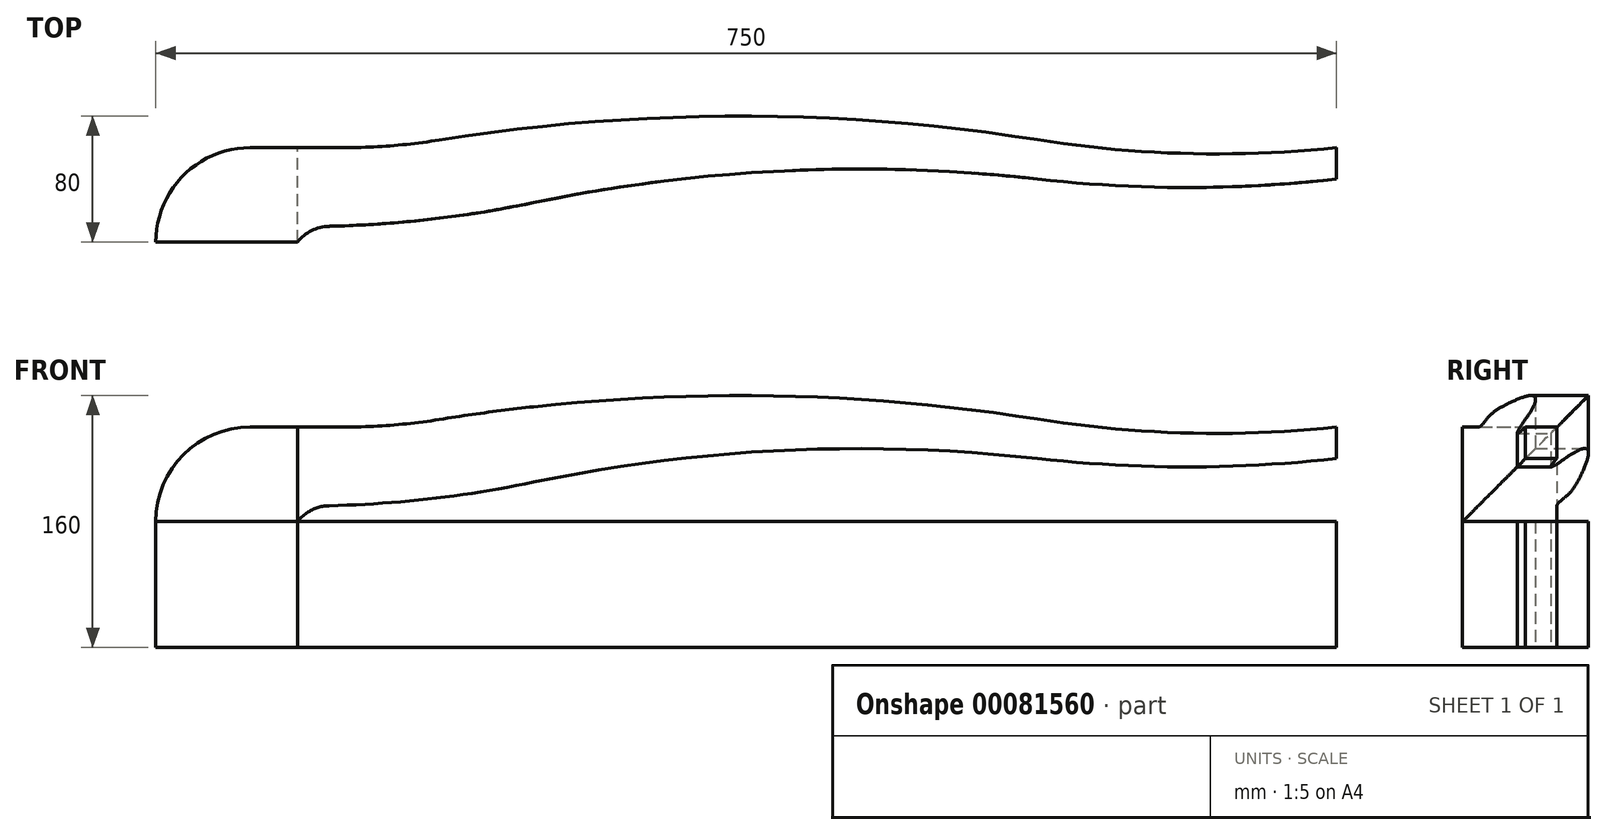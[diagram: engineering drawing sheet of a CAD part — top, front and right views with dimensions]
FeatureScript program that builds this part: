
annotation { "Feature Type Name" : "Feature", "Feature Type Description" : "" }
export const myFeature = defineFeature(function(context is Context, id is Id, definition is map)
    precondition{}
    {
        {
            var Q0;
            Q0=qCreatedBy(makeId("Front.planeOp"),FACE);
            var sketch = newSketch(context, id + "F0", { "sketchPlane" : qUnion([Q0])});
            skLineSegment(sketch, "E0.bottom", {"start": v(-375, 40) * mm, "end": v(375, 40) * mm, "construction": true});
            skLineSegment(sketch, "E0.top", {"start": v(-375, -40) * mm, "end": v(375, -40) * mm, "construction": true});
            skLineSegment(sketch, "E0.left", {"start": v(-375, 40) * mm, "end": v(-375, -40) * mm, "construction": true});
            skLineSegment(sketch, "E0.right", {"start": v(375, 40) * mm, "end": v(375, -40) * mm, "construction": true});
            skArc(sketch, "E1", {"start": v(-375, -40) * mm, "mid": v(-357.43, 2.43) * mm, "end": v(-315, 20) * mm});
            skLineSegment(sketch, "E2", {"start": v(-315, 20) * mm, "end": v(-255, 20) * mm});
            skArc(sketch, "E3", {"start": v(-255, 20) * mm, "mid": v(-224.9, 21.2) * mm, "end": v(-195, 24.79) * mm});
            skArc(sketch, "E4", {"start": v(-195, 24.79) * mm, "mid": v(-5, 40) * mm, "end": v(185, 25) * mm});
            skArc(sketch, "E5", {"start": v(185, 25) * mm, "mid": v(279.83, 16.23) * mm, "end": v(375, 20) * mm});
            skLineSegment(sketch, "E6", {"start": v(375, 20) * mm, "end": v(375, 0) * mm});
            skArc(sketch, "E7", {"start": v(375, 0) * mm, "mid": v(280, -5.33) * mm, "end": v(185, 0) * mm});
            skArc(sketch, "E8", {"start": v(185, 0) * mm, "mid": v(24.4, 5.23) * mm, "end": v(-135, -15) * mm});
            skArc(sketch, "E9", {"start": v(-135, -15) * mm, "mid": v(-199.66, -25.45) * mm, "end": v(-265, -30) * mm});
            skArc(sketch, "E10", {"start": v(-265, -30) * mm, "mid": v(-276.12, -32.77) * mm, "end": v(-285, -40) * mm});
            skLineSegment(sketch, "E11", {"start": v(-372.46, -190.94) * mm, "end": v(-262.22, 0) * mm, "construction": true});
            skLineSegment(sketch, "E12", {"start": v(-285, -40) * mm, "end": v(-375, -40) * mm});
            skSolve(sketch);
        }
        {
            var Q0;
            Q0 = qSketchRegion(id + "F0", true);
            extrude(context, id + "F1", {"entities" : qUnion([Q0]), "endBound" : BoundingType.SYMMETRIC, "depth" : 80 * mm});
        }
        {
            var Q0;
            Q0=makeQuery(id+"F1.opExtrude","SWEPT_BODY",BODY,{"disambiguationData":[OSD([sQuery(id+"F0.wireOp",EDGE,"E1"),sQuery(id+"F0.wireOp",EDGE,"E2"),sQuery(id+"F0.wireOp",EDGE,"E3"),sQuery(id+"F0.wireOp",EDGE,"E4"),sQuery(id+"F0.wireOp",EDGE,"E5"),sQuery(id+"F0.wireOp",EDGE,"E6"),sQuery(id+"F0.wireOp",EDGE,"E7"),sQuery(id+"F0.wireOp",EDGE,"E8"),sQuery(id+"F0.wireOp",EDGE,"E9"),sQuery(id+"F0.wireOp",EDGE,"E10"),sQuery(id+"F0.wireOp",EDGE,"E12")])]});
            var Q1;
            Q1=makeQuery(id+"F1.opExtrude","CAP_EDGE",EDGE,{"disambiguationData":[OSD([sQuery(id+"F0.wireOp",EDGE,"E12")])],"isStart":false});
            transform(context, id + "F2", {"entities" : qUnion([Q0]), "transformType" : TransformType.ROTATION, "transformAxis" : qUnion([Q1]), "angle" : 90 * degree, "makeCopy" : true});
        }
        {
            var Q0;
            Q0=makeQuery(id+"F2.opPattern","COPY",BODY,{"derivedFrom":makeQuery(id+"F1.opExtrude","SWEPT_BODY",BODY,{"disambiguationData":[OSD([sQuery(id+"F0.wireOp",EDGE,"E1"),sQuery(id+"F0.wireOp",EDGE,"E2"),sQuery(id+"F0.wireOp",EDGE,"E3"),sQuery(id+"F0.wireOp",EDGE,"E4"),sQuery(id+"F0.wireOp",EDGE,"E5"),sQuery(id+"F0.wireOp",EDGE,"E6"),sQuery(id+"F0.wireOp",EDGE,"E7"),sQuery(id+"F0.wireOp",EDGE,"E8"),sQuery(id+"F0.wireOp",EDGE,"E9"),sQuery(id+"F0.wireOp",EDGE,"E10"),sQuery(id+"F0.wireOp",EDGE,"E12")])]}),"instanceName":"1"});
            transform(context, id + "F3", {"entities" : qUnion([Q0]), "transformType" : TransformType.TRANSLATION_3D, "dx" : 0 * mm, "dy" : 0 * mm, "dz" : 80 * mm, "makeCopy" : true});
        }
        {
            var Q0;
            Q0=makeQuery(id+"F3.opPattern","COPY",BODY,{"derivedFrom":makeQuery(id+"F2.opPattern","COPY",BODY,{"derivedFrom":makeQuery(id+"F1.opExtrude","SWEPT_BODY",BODY,{"disambiguationData":[OSD([sQuery(id+"F0.wireOp",EDGE,"E1"),sQuery(id+"F0.wireOp",EDGE,"E2"),sQuery(id+"F0.wireOp",EDGE,"E3"),sQuery(id+"F0.wireOp",EDGE,"E4"),sQuery(id+"F0.wireOp",EDGE,"E5"),sQuery(id+"F0.wireOp",EDGE,"E6"),sQuery(id+"F0.wireOp",EDGE,"E7"),sQuery(id+"F0.wireOp",EDGE,"E8"),sQuery(id+"F0.wireOp",EDGE,"E9"),sQuery(id+"F0.wireOp",EDGE,"E10"),sQuery(id+"F0.wireOp",EDGE,"E12")])]}),"instanceName":"1"}),"instanceName":"1"});
            var Q1;
            Q1=makeQuery(id+"F1.opExtrude","SWEPT_BODY",BODY,{"disambiguationData":[OSD([sQuery(id+"F0.wireOp",EDGE,"E1"),sQuery(id+"F0.wireOp",EDGE,"E2"),sQuery(id+"F0.wireOp",EDGE,"E3"),sQuery(id+"F0.wireOp",EDGE,"E4"),sQuery(id+"F0.wireOp",EDGE,"E5"),sQuery(id+"F0.wireOp",EDGE,"E6"),sQuery(id+"F0.wireOp",EDGE,"E7"),sQuery(id+"F0.wireOp",EDGE,"E8"),sQuery(id+"F0.wireOp",EDGE,"E9"),sQuery(id+"F0.wireOp",EDGE,"E10"),sQuery(id+"F0.wireOp",EDGE,"E12")])]});
            booleanBodies(context, id + "F4", {"operationType" : BooleanOperationType.INTERSECTION, "tools" : qUnion([Q0, Q1])});
        }
        {
            var Q0;
            {var subQ0=makeQuery(id+"F1.opExtrude","SWEPT_BODY",BODY,{"disambiguationData":[OSD([sQuery(id+"F0.wireOp",EDGE,"E1"),sQuery(id+"F0.wireOp",EDGE,"E2"),sQuery(id+"F0.wireOp",EDGE,"E3"),sQuery(id+"F0.wireOp",EDGE,"E4"),sQuery(id+"F0.wireOp",EDGE,"E5"),sQuery(id+"F0.wireOp",EDGE,"E6"),sQuery(id+"F0.wireOp",EDGE,"E7"),sQuery(id+"F0.wireOp",EDGE,"E8"),sQuery(id+"F0.wireOp",EDGE,"E9"),sQuery(id+"F0.wireOp",EDGE,"E10"),sQuery(id+"F0.wireOp",EDGE,"E12")])]});Q0=makeQuery(id+"F4.opBoolean","INTERSECT",BODY,{"derivedFrom":[subQ0,makeQuery(id+"F3.opPattern","COPY",BODY,{"derivedFrom":makeQuery(id+"F2.opPattern","COPY",BODY,{"derivedFrom":subQ0,"instanceName":"1"}),"instanceName":"1"})]});}
            transform(context, id + "F5", {"entities" : qUnion([Q0]), "transformType" : TransformType.TRANSLATION_3D, "dx" : 0 * mm, "dy" : 0 * mm, "dz" : -1000 * mm, "makeCopy" : true});
        }
        {
            var Q0;
            {var subQ0=makeQuery(id+"F1.opExtrude","SWEPT_BODY",BODY,{"disambiguationData":[OSD([sQuery(id+"F0.wireOp",EDGE,"E1"),sQuery(id+"F0.wireOp",EDGE,"E2"),sQuery(id+"F0.wireOp",EDGE,"E3"),sQuery(id+"F0.wireOp",EDGE,"E4"),sQuery(id+"F0.wireOp",EDGE,"E5"),sQuery(id+"F0.wireOp",EDGE,"E6"),sQuery(id+"F0.wireOp",EDGE,"E7"),sQuery(id+"F0.wireOp",EDGE,"E8"),sQuery(id+"F0.wireOp",EDGE,"E9"),sQuery(id+"F0.wireOp",EDGE,"E10"),sQuery(id+"F0.wireOp",EDGE,"E12")])]});Q0=makeQuery(id+"F5.opPattern","COPY",BODY,{"derivedFrom":makeQuery(id+"F4.opBoolean","INTERSECT",BODY,{"derivedFrom":[subQ0,makeQuery(id+"F3.opPattern","COPY",BODY,{"derivedFrom":makeQuery(id+"F2.opPattern","COPY",BODY,{"derivedFrom":subQ0,"instanceName":"1"}),"instanceName":"1"})]}),"instanceName":"1"});}
            deleteBodies(context, id + "F6", {"entities" : qUnion([Q0])});
        }
    });
